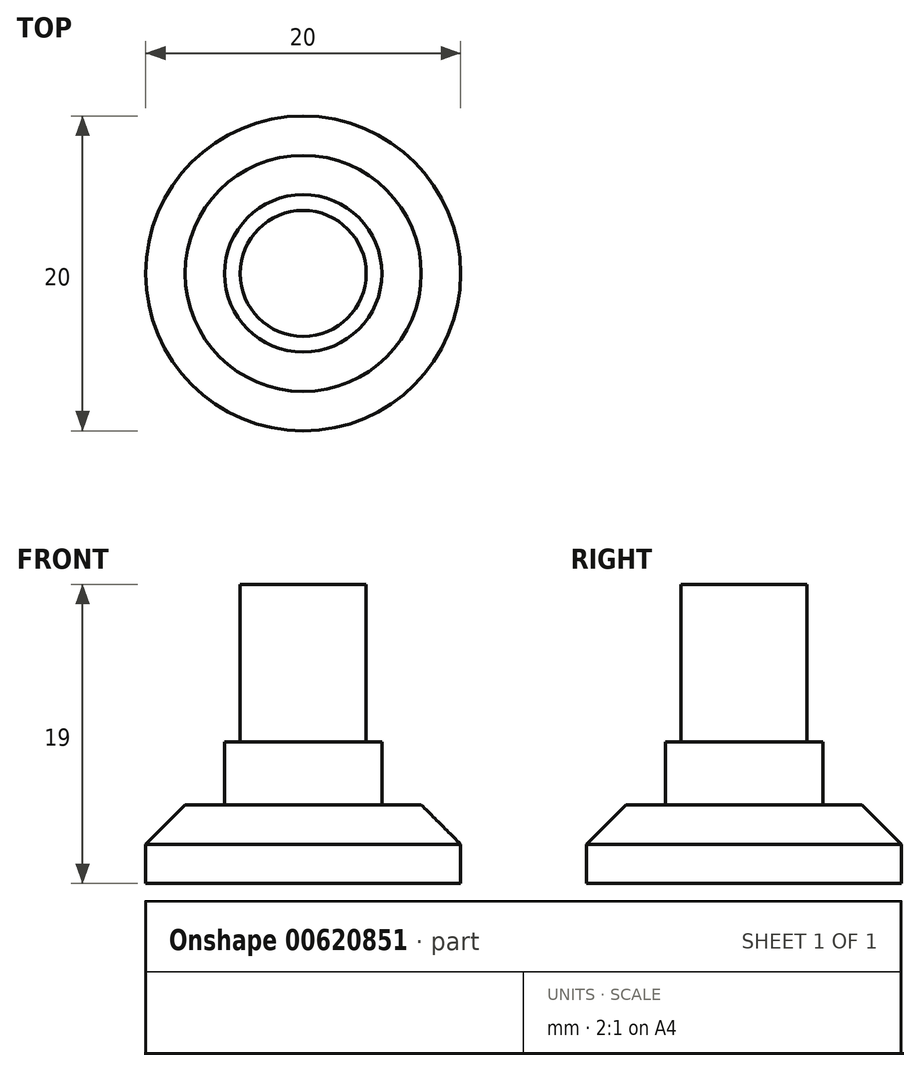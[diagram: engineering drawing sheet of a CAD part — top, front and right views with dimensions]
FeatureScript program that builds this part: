
annotation { "Feature Type Name" : "Feature", "Feature Type Description" : "" }
export const myFeature = defineFeature(function(context is Context, id is Id, definition is map)
    precondition{}
    {
        {
            var Q0;
            Q0=qCreatedBy(makeId("Top.planeOp"),FACE);
            var sketch = newSketch(context, id + "F0", { "sketchPlane" : qUnion([Q0])});
            skCircle(sketch, "E0", {"center": v(0, 0) * mm, "radius": 10 * mm});
            skSolve(sketch);
        }
        {
            var Q0;
            Q0=makeQuery(id+"F0.imprint","IMPRINT",FACE,{"disambiguationData":[TD([[makeQuery(id+"F0.imprint","IMPRINT",EDGE,{"derivedFrom":sQuery(id+"F0.wireOp",EDGE,"E0")}),1.0]])]});
            extrude(context, id + "F1", {"entities" : qUnion([Q0]), "depth" : 5 * mm, "offsetDistance" : 25 * mm});
        }
        {
            var Q0;
            Q0=makeQuery(id+"F1.opExtrude","CAP_FACE",FACE,{"disambiguationData":[OSD([sQuery(id+"F0.wireOp",EDGE,"E0")])],"isStart":false});
            var sketch = newSketch(context, id + "F2", { "sketchPlane" : qUnion([Q0])});
            skCircle(sketch, "E1", {"center": v(0, 0) * mm, "radius": 5 * mm});
            skSolve(sketch);
        }
        {
            var Q0;
            Q0 = qSketchRegion(id + "F2", true);
            extrude(context, id + "F3", {"entities" : qUnion([Q0]), "operationType" : NewBodyOperationType.ADD, "depth" : 4 * mm, "offsetDistance" : 25 * mm});
        }
        {
            var Q0;
            Q0=makeQuery(id+"F3.opExtrude","CAP_FACE",FACE,{"disambiguationData":[OSD([sQuery(id+"F2.wireOp",EDGE,"E1")])],"isStart":false});
            var sketch = newSketch(context, id + "F4", { "sketchPlane" : qUnion([Q0])});
            skCircle(sketch, "E2", {"center": v(0, 0) * mm, "radius": 4 * mm});
            skSolve(sketch);
        }
        {
            var Q0;
            Q0=makeQuery(id+"F4.imprint","IMPRINT",FACE,{"disambiguationData":[TD([[makeQuery(id+"F4.imprint","IMPRINT",EDGE,{"derivedFrom":sQuery(id+"F4.wireOp",EDGE,"E2")}),1.0]])]});
            extrude(context, id + "F5", {"entities" : qUnion([Q0]), "operationType" : NewBodyOperationType.ADD, "depth" : 10 * mm, "offsetDistance" : 25 * mm});
        }
        {
            var Q0;
            Q0=makeQuery(id+"F1.opExtrude","CAP_EDGE",EDGE,{"disambiguationData":[OSD([sQuery(id+"F0.wireOp",EDGE,"E0")])],"isStart":false});
            chamfer(context, id + "F6", {"entities" : qUnion([Q0]), "width" : 2.5 * mm, "tangentPropagation" : true});
        }
    });
